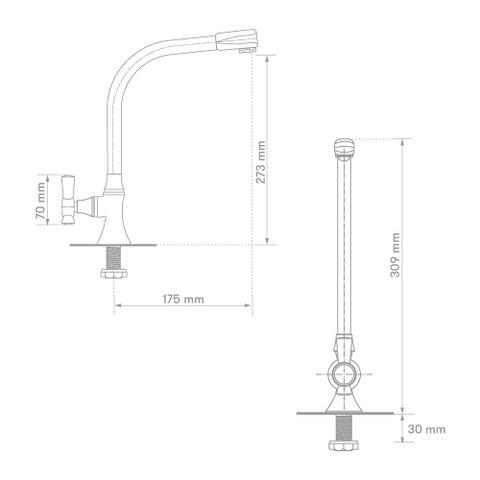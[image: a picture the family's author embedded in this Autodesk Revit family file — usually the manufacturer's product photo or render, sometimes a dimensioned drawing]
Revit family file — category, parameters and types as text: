
# Revit family: 01-1360-11-LLAVE MÓVIL MESA ATLANTICO
name_source: partatom
category: Plumbing Fixtures
revit_build: Autodesk Revit 2018 (Build: 20170223_1515(x64)
units: mm (PartAtom-declared; Revit-internal decimal feet)

## family parameters
Cut with Voids When Loaded = No
Host = Face
OmniClass Number = 23.31.11.00
Part Type = Normal
Room Calculation Point = No
Round Connector Dimension = Use Diameter
Shared = No

## types (1)
- 01-1360-11
    Alto = 306 mm
    Alto Aireador = 239 mm  [stored 0.784121 ft]
    Ancho = 74 mm
    CW Connection = Yes
    Default Elevation = 0 mm  [stored 0 ft]
    Description = Monomando
    HW Connection = Yes
    Link Ficha Tecnica = https://infotecnica.gricol.com
    Manija = 66 mm  [stored 0.216535 ft]
    Manufacturer = Gricol
    Model = 01-1360-11
    Plastico ABS Cromado = Plastico - ABS Cromado
    Product Name = LLAVE MOVIL MESA ATLANTICO
    Profundidad = 162 mm  [stored 0.531496 ft]
    Type Image = 01-1360-11-FOTO LLAVE MOVIL MESA ATLANTICO.jpg
    URL = https://www.gricol.com
    Vent Connection = No
    Waste Connection = No

note: [stored X ft] marks values corroborated as IEEE doubles in the binary element streams (Revit-internal decimal feet)

## geometry (parser evidence)
native form markers: Blend x2, Sweep x10
no freeform markers — native parametric forms only
